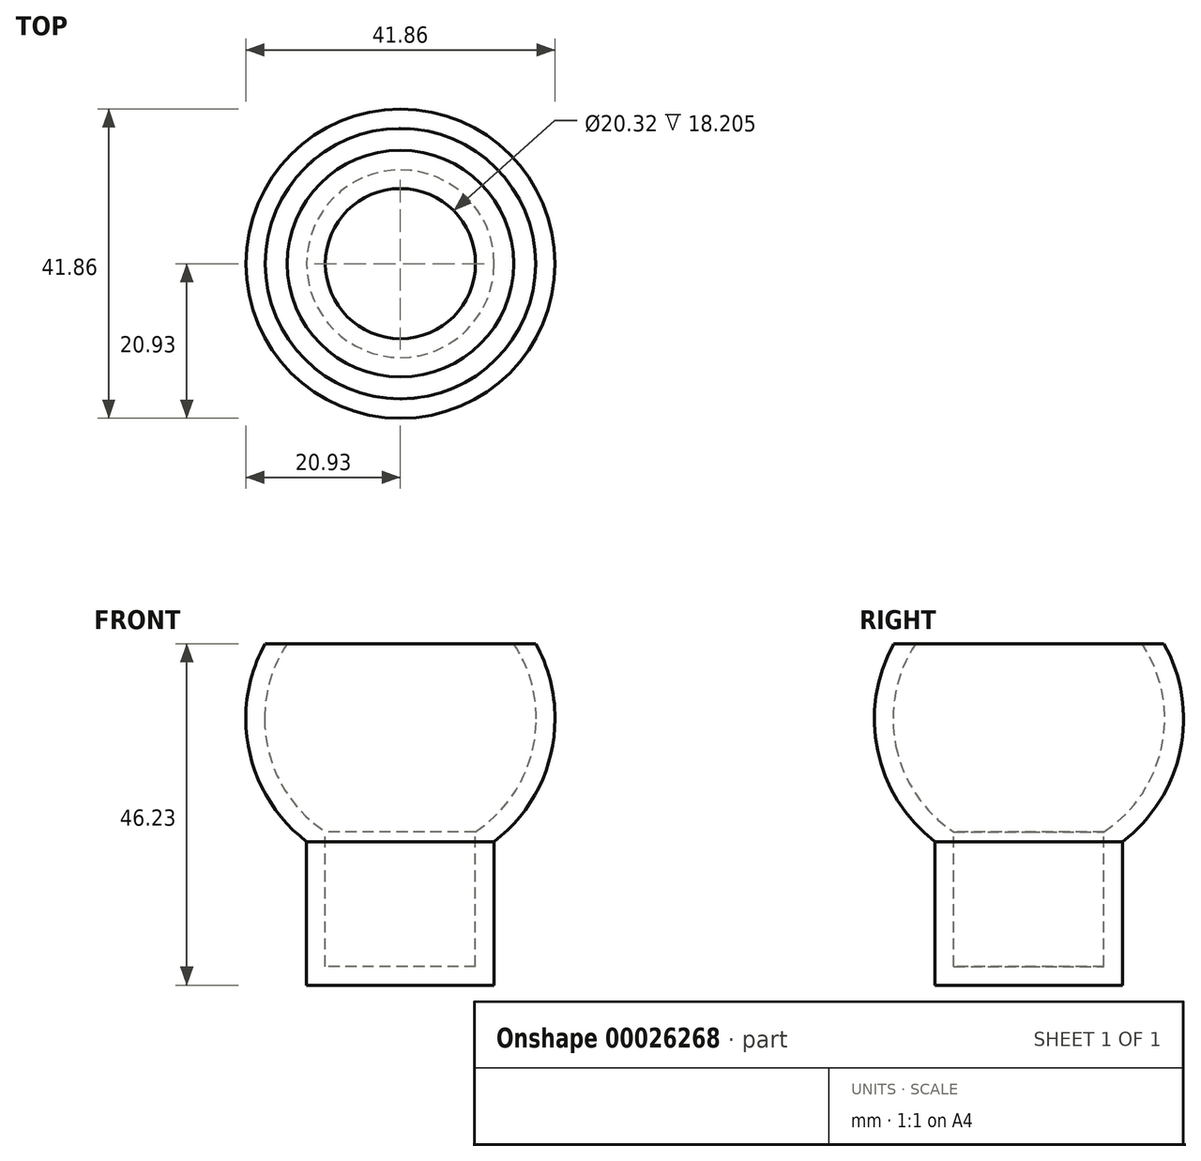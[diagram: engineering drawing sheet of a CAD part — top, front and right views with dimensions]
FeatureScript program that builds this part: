
annotation { "Feature Type Name" : "Feature", "Feature Type Description" : "" }
export const myFeature = defineFeature(function(context is Context, id is Id, definition is map)
    precondition{}
    {
        {
            var Q0;
            Q0=qCreatedBy(makeId("Top.planeOp"),FACE);
            var sketch = newSketch(context, id + "F0", { "sketchPlane" : qUnion([Q0])});
            skCircle(sketch, "E0", {"center": v(0, 0) * mm, "radius": 12.7 * mm});
            skSolve(sketch);
        }
        {
            var Q0;
            Q0 = qSketchRegion(id + "F0", true);
            extrude(context, id + "F1", {"entities" : qUnion([Q0]), "oppositeDirection" : true, "depth" : 23.37 * mm});
        }
        {
            var Q0;
            Q0=qCreatedBy(makeId("Right.planeOp"),FACE);
            var sketch = newSketch(context, id + "F2", { "sketchPlane" : qUnion([Q0])});
            skCircle(sketch, "E1", {"center": v(0, 12.7) * mm, "radius": 20.93 * mm});
            skLineSegment(sketch, "E2", {"start": v(0, 12.7) * mm, "end": v(0, 22.86) * mm});
            skLineSegment(sketch, "E3", {"start": v(0, 22.86) * mm, "end": v(-18.3, 22.86) * mm});
            skLineSegment(sketch, "E4", {"start": v(0, 22.86) * mm, "end": v(18.3, 22.86) * mm});
            skLineSegment(sketch, "E5", {"start": v(0, 12.7) * mm, "end": v(0, 0) * mm});
            skSolve(sketch);
        }
        {
            var Q0;
            {var subQ1=sQuery(id+"F2.wireOp",EDGE,"E3");Q0=makeQuery(id+"F2.imprint","IMPRINT",FACE,{"disambiguationData":[TD([[makeQuery(id+"F2.imprint","IMPRINT",EDGE,{"derivedFrom":subQ1}),1.0]])]});}
            extrude(context, id + "F3", {"entities" : qUnion([Q0]), "operationType" : NewBodyOperationType.ADD, "endBound" : BoundingType.SYMMETRIC, "depth" : 41.86 * mm});
        }
        {
            var Q0;
            Q0=makeQuery(id+"F3.opExtrude","CAP_EDGE",EDGE,{"disambiguationData":[OSD([sQuery(id+"F2.wireOp",EDGE,"E1")])],"isStart":true});
            var Q1;
            Q1=makeQuery(id+"F3.opExtrude","CAP_EDGE",EDGE,{"disambiguationData":[OSD([sQuery(id+"F2.wireOp",EDGE,"E1")])],"isStart":false});
            fillet(context, id + "F4", {"entities" : qUnion([Q0, Q1]), "radius" : 20.93 * mm, "tangentPropagation" : true, "allowEdgeOverflow" : false});
        }
        {
            var Q0;
            Q0=makeQuery(id+"F3.opExtrude","SWEPT_FACE",FACE,{"disambiguationData":[OSD([sQuery(id+"F2.wireOp",EDGE,"E3"),sQuery(id+"F2.wireOp",EDGE,"E4")])]});
            shell(context, id + "F5", {"entities" : qUnion([Q0]), "thickness" : 2.54 * mm});
        }
    });
